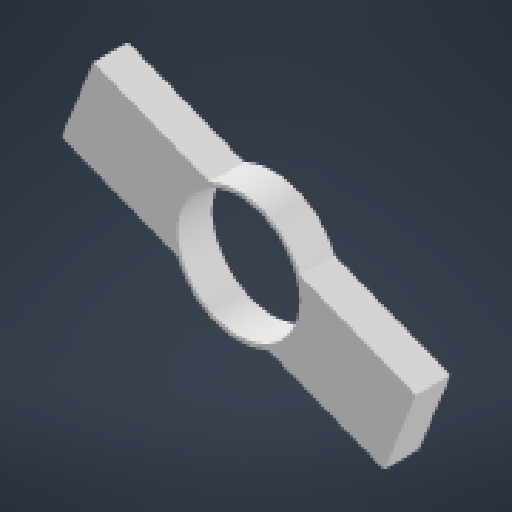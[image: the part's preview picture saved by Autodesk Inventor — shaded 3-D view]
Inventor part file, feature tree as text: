
AUTODESK INVENTOR PART (.ipt)
format: ipt  version: 2024.2 (Build 282272000, 272)  size: 348,160 bytes
history: native  units: in
note: dims shown in document units (in); Inventor stores cm internally (conversion verified against a paired STEP export)
features: extrude x7, sketch x6, fillet x6, other x5, reference x4, plane x3, projected_geometry x2
ambient origin geometry x8: Origin, YZ Plane, XZ Plane, XY Plane, X Axis, Y Axis, Z Axis, Center Point
bodies: Solid1 (feature_tree)
feature tree (33):
  sketch  "Sketch1"  dims[d0=0.1969in d1=0.1969in]
  plane  "Work Plane1"
  extrude  "Extrusion1"  Depth=0.1969in
  extrude  "Extrusion2"  Depth=0.7874in
  extrude  "Extrusion3"  TaperAngle=0.0deg  [1 undecoded]
  plane  "Work Plane2"
  extrude  "Extrusion4"  Depth=0.0394in
  extrude  "Extrusion5"  Depth=1.0in TaperAngle=0.0deg
  fillet  "Fillet1"  Radius=0.629in
  fillet  "Fillet2"  Radius=0.1083in
  fillet  "Fillet3"  Radius=0.1693in
  fillet  "Fillet4"  Radius=0.3543in
  fillet  "Fillet5"  [1 undecoded]
  fillet  "Fillet6"  Radius=0.1181in
  plane  "Work Plane3"
  sketch  "Sketch6"  dims[d27=0.125in d28=0.0312in d29=0.0625in d30=0.0625in d31=0.0625in d32=0.0625in d33=0.1693in d34=0.315in d35=0.0in d36=0.2362in d37=0.0in d38=0.0in d39=0.0in d40=0.9413in d41=0.0in]
  extrude  "Extrusion6"  Depth=0.9413in
  extrude  "Extrusion7"  Depth=0.0625in
  reference  "Reference1"
  reference  "Reference2"
  reference  "Reference3"
  sketch  "Sketch2"  dims[d2=0.7874in d3=0.7874in]
  sketch  "Sketch3"  dims[d4=0.0in d5=0.0in]
  sketch  "Sketch4"  dims[d6=1.0in d7=0.0in d8=0.0394in]
  reference  "Reference4"
  sketch  "Sketch5"  dims[d10=1.0in d11=0.0in d16=1.0in d17=0.0in d19=0.629in d20=0.1083in d21=0.0in d22=0.1693in d23=0.3543in d24=0.0in d25=0.0in d26=0.1181in]
  other  "<userpath>\Desktop\Robotics\Swerve2\Assemblies\Pod.iam"
  other  "Pod.iam"
  other  "Wheel_Base:1"
  projected_geometry  "Project Cut Edges1"
  projected_geometry  "Project Cut Edges2"
  other  "2106 Series Stainless Steel REX Shaft (8mm Diameter, 40mm Length):1"
  other  "Inner_Pod_Holder:1"
note: 2 required parameter values undecoded (feature->parameter linkage not recoverable at this tier; creation-order binding heuristic only, values carry confidence <= 0.55)
